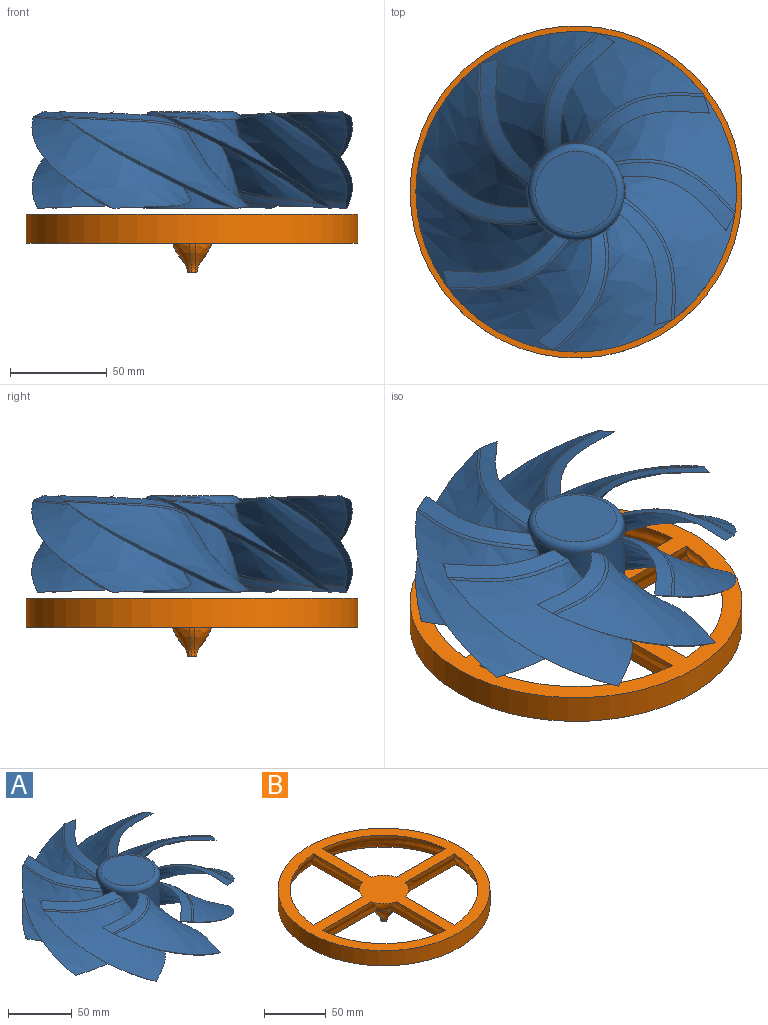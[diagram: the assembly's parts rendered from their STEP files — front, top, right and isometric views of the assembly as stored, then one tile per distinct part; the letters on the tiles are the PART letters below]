
ASSEMBLY  parts=2 mates=1
PART A: 78 faces, bbox 171.9x171.9x56.8 mm
  f0: plane 1.11x1.04mm, normal (0,0,1), area 0.1mm2, adj f1,f2,f6
  f1: bspline ~100.45x78.36mm, area 4222.1mm2, adj f0,f2,f6,f7,f9
  f2: bspline ~105.04x56.82mm, area 369.9mm2, adj f0,f1,f3,f5,f6,f7,f8
  f3: bspline ~102.44x86.17mm, area 4384.7mm2, adj f2,f4,f5,f8
  f4: bspline ~45.45x24.65mm, area 25.1mm2, adj f3,f5,f8,f9
  f5: bspline ~56.72x53.67mm, area 536.9mm2, adj f2,f3,f4,f7,f9
  f6: bspline ~66.83x38.35mm, area 557.3mm2, adj f0,f1,f2,f8,f9
  f7: bspline ~42.83x42.33mm, area 111mm2, adj f1,f2,f5,f9
  f8: bspline ~64.89x29.3mm, area 129.9mm2, adj f2,f3,f4,f6,f9
  f9: cylinder r=25mm len=50mm, axis (0,0,-1), area 5743.7mm2, adj f1,f4,f5,f6,f7,f8,f11,f14
  f10: plane 1.48x0.11mm, normal (0,0,1), area 0.1mm2, adj f11,f12,f16
  f11: bspline ~100.66x62.25mm, area 4222.1mm2, adj f9,f10,f12,f16,f17
  f12: bspline ~98.13x56.82mm, area 369.9mm2, adj f10,f11,f13,f15,f16,f17,f18
  f13: bspline ~106.86x66.9mm, area 4384.7mm2, adj f12,f14,f15,f18
  f14: bspline ~45.45x26.34mm, area 25.1mm2, adj f9,f13,f15,f18
  f15: bspline ~71.2x23.02mm, area 536.9mm2, adj f9,f12,f13,f14,f17
  f16: bspline ~68.89x33.4mm, area 557.3mm2, adj f9,f10,f11,f12,f18
  f17: bspline ~59.7x10.88mm, area 111mm2, adj f9,f11,f12,f15
  f18: bspline ~64.75x28.94mm, area 129.9mm2, adj f9,f12,f13,f14,f16
  f19: plane 1.11x1.04mm, normal (0,0,1), area 0.1mm2, adj f20,f21,f25
  f20: bspline ~100.45x78.36mm, area 4222.1mm2, adj f9,f19,f21,f25,f26
  f21: bspline ~105.04x56.82mm, area 369.9mm2, adj f19,f20,f22,f24,f25,f26,f27
  f22: bspline ~102.44x86.17mm, area 4384.7mm2, adj f21,f23,f24,f27
  f23: bspline ~45.45x24.65mm, area 25.1mm2, adj f9,f22,f24,f27
  f24: bspline ~56.72x53.67mm, area 536.9mm2, adj f9,f21,f22,f23,f26
  f25: bspline ~66.83x38.35mm, area 557.3mm2, adj f9,f19,f20,f21,f27
  f26: bspline ~42.83x42.33mm, area 111mm2, adj f9,f20,f21,f24
  f27: bspline ~64.89x29.3mm, area 129.9mm2, adj f9,f21,f22,f23,f25
  f28: plane 1.48x0.11mm, normal (0,0,1), area 0.1mm2, adj f29,f30,f34
  f29: bspline ~100.66x62.25mm, area 4222.1mm2, adj f9,f28,f30,f34,f35
  f30: bspline ~98.13x56.82mm, area 369.9mm2, adj f28,f29,f31,f33,f34,f35,f36
  f31: bspline ~106.86x66.9mm, area 4384.7mm2, adj f30,f32,f33,f36
  f32: bspline ~45.45x26.34mm, area 25.1mm2, adj f9,f31,f33,f36
  f33: bspline ~71.2x23.02mm, area 536.9mm2, adj f9,f30,f31,f32,f35
  f34: bspline ~68.89x33.4mm, area 557.3mm2, adj f9,f28,f29,f30,f36
  f35: bspline ~59.7x10.88mm, area 111mm2, adj f9,f29,f30,f33
  f36: bspline ~64.75x28.94mm, area 129.9mm2, adj f9,f30,f31,f32,f34
  f37: plane 1.11x1.04mm, normal (0,0,1), area 0.1mm2, adj f38,f39,f43
  f38: bspline ~100.45x78.36mm, area 4222.1mm2, adj f9,f37,f39,f43,f44
  f39: bspline ~105.04x56.82mm, area 369.9mm2, adj f37,f38,f40,f42,f43,f44,f45
  f40: bspline ~102.44x86.17mm, area 4384.7mm2, adj f39,f41,f42,f45
  f41: bspline ~45.45x24.65mm, area 25.1mm2, adj f9,f40,f42,f45
  f42: bspline ~56.72x53.67mm, area 536.9mm2, adj f9,f39,f40,f41,f44
  f43: bspline ~66.83x38.35mm, area 557.3mm2, adj f9,f37,f38,f39,f45
  f44: bspline ~42.83x42.33mm, area 111mm2, adj f9,f38,f39,f42
  f45: bspline ~64.89x29.3mm, area 129.9mm2, adj f9,f39,f40,f41,f43
  f46: plane 1.48x0.11mm, normal (0,0,1), area 0.1mm2, adj f47,f48,f52
  f47: bspline ~100.66x62.25mm, area 4222.1mm2, adj f9,f46,f48,f52,f53
  f48: bspline ~98.13x56.82mm, area 369.9mm2, adj f46,f47,f49,f51,f52,f53,f54
  f49: bspline ~106.86x66.9mm, area 4384.7mm2, adj f48,f50,f51,f54
  f50: bspline ~45.45x26.34mm, area 25.1mm2, adj f9,f49,f51,f54
  f51: bspline ~71.2x23.02mm, area 536.9mm2, adj f9,f48,f49,f50,f53
  f52: bspline ~68.89x33.4mm, area 557.3mm2, adj f9,f46,f47,f48,f54
  f53: bspline ~59.7x10.88mm, area 111mm2, adj f9,f47,f48,f51
  f54: bspline ~64.75x28.94mm, area 129.9mm2, adj f9,f48,f49,f50,f52
  f55: plane 1.11x1.04mm, normal (0,0,1), area 0.1mm2, adj f56,f57,f61
  f56: bspline ~100.45x78.36mm, area 4222.1mm2, adj f9,f55,f57,f61,f62
  f57: bspline ~105.04x56.82mm, area 369.9mm2, adj f55,f56,f58,f60,f61,f62,f63
  f58: bspline ~102.44x86.17mm, area 4384.7mm2, adj f57,f59,f60,f63
  f59: bspline ~45.45x24.65mm, area 25.1mm2, adj f9,f58,f60,f63
  f60: bspline ~56.72x53.67mm, area 536.9mm2, adj f9,f57,f58,f59,f62
  f61: bspline ~66.83x38.35mm, area 557.3mm2, adj f9,f55,f56,f57,f63
  f62: bspline ~42.83x42.33mm, area 111mm2, adj f9,f56,f57,f60
  f63: bspline ~64.89x29.3mm, area 129.9mm2, adj f9,f57,f58,f59,f61
  f64: plane 1.48x0.11mm, normal (0,0,1), area 0.1mm2, adj f65,f66,f70
  f65: bspline ~100.66x62.25mm, area 4222.1mm2, adj f9,f64,f66,f70,f71
  f66: bspline ~98.13x56.82mm, area 369.9mm2, adj f64,f65,f67,f69,f70,f71,f72
  f67: bspline ~106.86x66.9mm, area 4384.7mm2, adj f66,f68,f69,f72
  f68: bspline ~45.45x26.34mm, area 25.1mm2, adj f9,f67,f69,f72
  f69: bspline ~71.2x23.02mm, area 536.9mm2, adj f9,f66,f67,f68,f71
  f70: bspline ~68.89x33.4mm, area 557.3mm2, adj f9,f64,f65,f66,f72
  f71: bspline ~59.7x10.88mm, area 111mm2, adj f9,f65,f66,f69
  f72: bspline ~64.75x28.94mm, area 129.9mm2, adj f9,f66,f67,f68,f70
  f73: cylinder r=22mm len=44mm, axis (0,0,-1), area 2349.9mm2, adj f74,f75
  f74: plane 50x50mm, normal (0,0,-1), area 443mm2, adj f9,f73
  f75: plane 44x44mm, normal (0,0,-1), area 1520.5mm2, adj f73
  f76: plane 42x42mm, normal (0,0,1), area 1385.4mm2, adj f77
  f77: torus R=21mm, axis (0,0,1), area 929.6mm2, adj f9,f76
PART B: 28 faces, bbox 172x172x30 mm
  f0: bspline ~18.27x18.27mm, area 286.7mm2, adj f4,f7,f11,f26
  f1: bspline ~18.27x18.27mm, area 286.7mm2, adj f4,f9,f10,f24
  f2: bspline ~18.27x18.27mm, area 286.7mm2, adj f4,f6,f13,f20
  f3: plane 172x172mm, normal (0,0,-1), area 3475.6mm2, adj f6,f7,f8,f9,f10,f11,f12,f13
  f4: plane 172x172mm, normal (0,0,1), area 8592.2mm2, adj f0,f1,f2,f5,f6,f7,f8,f9
  f5: bspline ~18.27x18.27mm, area 286.7mm2, adj f4,f8,f12,f22
  f6: extruded ~71.1x15mm, area 1009.6mm2, adj f2,f3,f4,f16
  f7: extruded ~71.1x15mm, area 1009.6mm2, adj f0,f3,f4,f14
  f8: extruded ~71.1x15mm, area 1009.6mm2, adj f3,f4,f5,f17
  f9: extruded ~71.1x15mm, area 1009.6mm2, adj f1,f3,f4,f15
  f10: extruded ~71.1x15mm, area 1009.6mm2, adj f1,f3,f4,f15
  f11: extruded ~71.1x15mm, area 1009.6mm2, adj f0,f3,f4,f14
  f12: extruded ~71.1x15mm, area 1009.6mm2, adj f3,f4,f5,f17
  f13: extruded ~71.1x15mm, area 1009.6mm2, adj f2,f3,f4,f16
  f14: revolved ~79.58x79.58mm, area 1885.5mm2, adj f3,f4,f7,f11
  f15: revolved ~79.58x79.58mm, area 1885.5mm2, adj f3,f4,f9,f10
  f16: revolved ~79.58x79.58mm, area 1885.5mm2, adj f3,f4,f6,f13
  f17: revolved ~79.58x79.58mm, area 1885.5mm2, adj f3,f4,f8,f12
  f18: cylinder r=86mm len=172mm, axis (0,0,-1), area 8105.3mm2, adj f3,f4
  f19: plane 5.01x5.01mm, normal (0,0,-1), area 19.6mm2, adj f20,f21,f22,f23,f24,f25,f26,f27
  f20: bspline ~15x9.51mm, area 124.9mm2, adj f2,f19,f21,f27
  f21: bspline ~15x7.99mm, area 42.2mm2, adj f3,f19,f20,f22
  f22: bspline ~15x9.51mm, area 124.9mm2, adj f5,f19,f21,f23
  f23: bspline ~15x7.99mm, area 42.2mm2, adj f3,f19,f22,f24
  f24: bspline ~15x9.51mm, area 124.9mm2, adj f1,f19,f23,f25
  f25: bspline ~15x7.99mm, area 42.2mm2, adj f3,f19,f24,f26
  f26: bspline ~15x9.51mm, area 124.9mm2, adj f0,f19,f25,f27
  f27: bspline ~15x7.99mm, area 42.2mm2, adj f3,f19,f20,f26
PLACE A t=(0,0,-2)mm
PLACE B t=(0,0,-20)mm
MATE revolute A.f9 <-> B.f18  axis (0,0,-1) through (0,0,-5)mm
